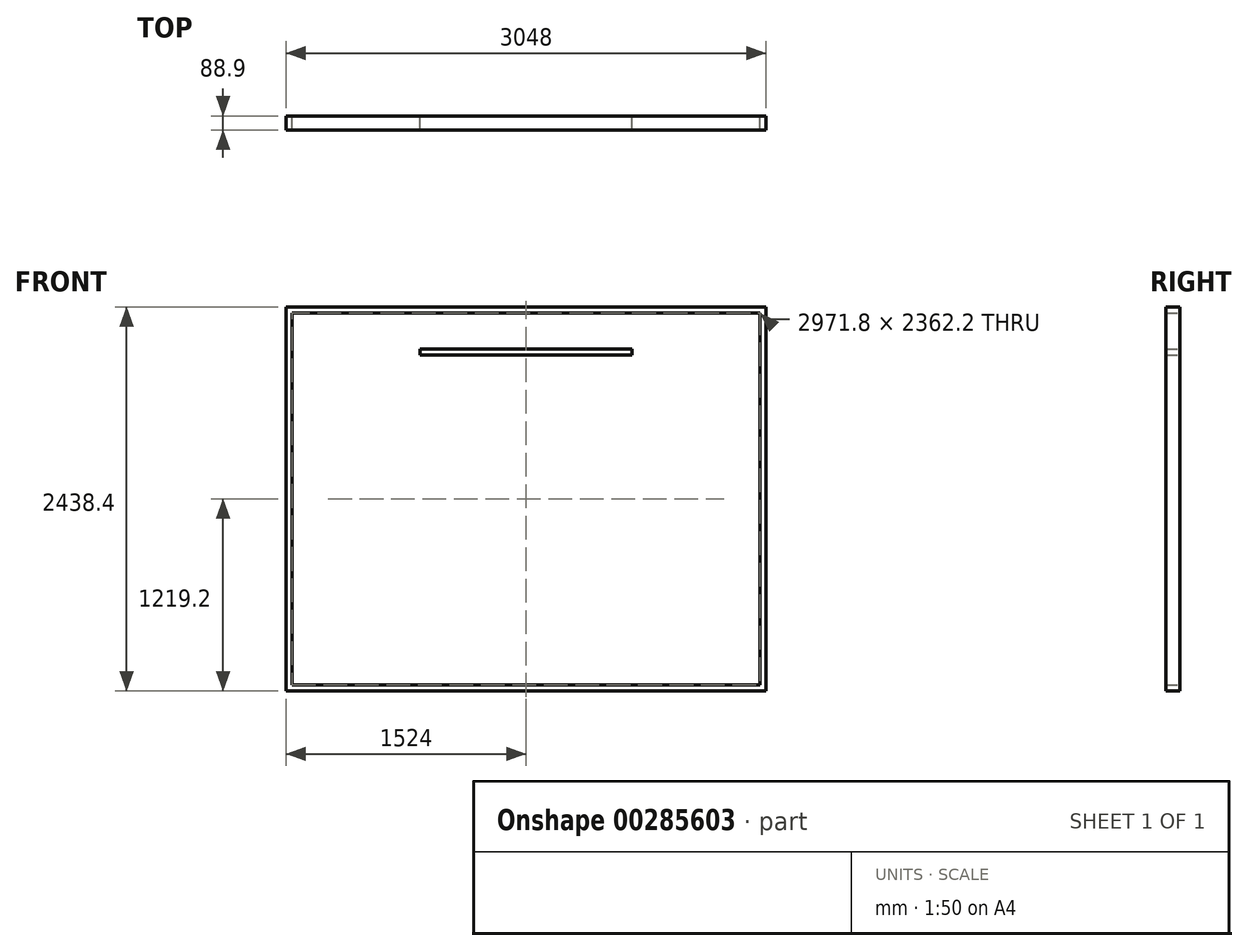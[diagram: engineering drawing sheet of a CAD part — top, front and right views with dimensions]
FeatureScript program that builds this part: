
annotation { "Feature Type Name" : "Feature", "Feature Type Description" : "" }
export const myFeature = defineFeature(function(context is Context, id is Id, definition is map)
    precondition{}
    {
        {
            var Q0;
            Q0=qCreatedBy(makeId("Front.planeOp"),FACE);
            var sketch = newSketch(context, id + "F0", { "sketchPlane" : qUnion([Q0])});
            skLineSegment(sketch, "E0.bottom", {"start": v(1485.9, -1219.2) * mm, "end": v(-1485.9, -1219.2) * mm});
            skLineSegment(sketch, "E0.left", {"start": v(1485.9, -1219.2) * mm, "end": v(1485.9, 1143) * mm});
            skLineSegment(sketch, "E0.right", {"start": v(-1485.9, -1219.2) * mm, "end": v(-1485.9, 1143) * mm});
            skPoint(sketch, "E0.middle", {"position": v(0, 0) * mm});
            skLineSegment(sketch, "E1.bottom", {"start": v(-1524, -1257.3) * mm, "end": v(1524, -1257.3) * mm});
            skLineSegment(sketch, "E1.left", {"start": v(-1524, -1257.3) * mm, "end": v(-1524, 1143) * mm});
            skLineSegment(sketch, "E1.right", {"start": v(1524, -1257.3) * mm, "end": v(1524, 1181.1) * mm});
            skLineSegment(sketch, "E2", {"start": v(1485.9, -1219.2) * mm, "end": v(1524, -1219.2) * mm});
            skLineSegment(sketch, "E3", {"start": v(-1485.9, -1219.2) * mm, "end": v(-1524, -1219.2) * mm});
            skLineSegment(sketch, "E4", {"start": v(-1524, -1219.2) * mm, "end": v(-1117.6, -1219.2) * mm});
            skLineSegment(sketch, "E5", {"start": v(-1117.6, -1219.2) * mm, "end": v(-711.2, -1219.2) * mm});
            skLineSegment(sketch, "E6", {"start": v(-711.2, -1219.2) * mm, "end": v(-304.8, -1219.2) * mm});
            skLineSegment(sketch, "E7", {"start": v(1524, -1219.2) * mm, "end": v(1117.6, -1219.2) * mm});
            skLineSegment(sketch, "E8", {"start": v(1117.6, -1219.2) * mm, "end": v(711.2, -1219.2) * mm});
            skLineSegment(sketch, "E9", {"start": v(711.2, -1219.2) * mm, "end": v(304.8, -1219.2) * mm});
            skLineSegment(sketch, "E10", {"start": v(304.8, -1219.2) * mm, "end": v(0, -1219.2) * mm});
            skLineSegment(sketch, "E11.bottom", {"start": v(-1117.6, -1219.2) * mm, "end": v(-1079.5, -1219.2) * mm});
            skLineSegment(sketch, "E11.left", {"start": v(-1117.6, -1219.2) * mm, "end": v(-1117.6, 1143) * mm});
            skLineSegment(sketch, "E11.right", {"start": v(-1079.5, -1219.2) * mm, "end": v(-1079.5, 1143) * mm});
            skLineSegment(sketch, "E12.bottom", {"start": v(-711.2, -1219.2) * mm, "end": v(-673.1, -1219.2) * mm});
            skLineSegment(sketch, "E12.left", {"start": v(-711.2, -1219.2) * mm, "end": v(-711.2, 1143) * mm});
            skLineSegment(sketch, "E13.bottom", {"start": v(1117.6, -1219.2) * mm, "end": v(1079.5, -1219.2) * mm});
            skLineSegment(sketch, "E13.left", {"start": v(1117.6, -1219.2) * mm, "end": v(1117.6, 1143) * mm});
            skLineSegment(sketch, "E13.right", {"start": v(1079.5, -1219.2) * mm, "end": v(1079.5, 1143) * mm});
            skLineSegment(sketch, "E14.bottom", {"start": v(711.2, -1219.2) * mm, "end": v(673.1, -1219.2) * mm});
            skLineSegment(sketch, "E14.left", {"start": v(711.2, -1219.2) * mm, "end": v(711.2, 1143) * mm});
            skLineSegment(sketch, "E15.top", {"start": v(673.1, -38.1) * mm, "end": v(-673.1, -38.1) * mm});
            skLineSegment(sketch, "E16.bottom", {"start": v(-673.1, -38.1) * mm, "end": v(673.1, -38.1) * mm});
            skLineSegment(sketch, "E16.top", {"start": v(-673.1, -76.2) * mm, "end": v(673.1, -76.2) * mm});
            skLineSegment(sketch, "E16.left", {"start": v(-673.1, -38.1) * mm, "end": v(-673.1, -76.2) * mm});
            skLineSegment(sketch, "E16.right", {"start": v(673.1, -38.1) * mm, "end": v(673.1, -76.2) * mm});
            skLineSegment(sketch, "E17.bottom", {"start": v(-304.8, -1219.2) * mm, "end": v(-266.7, -1219.2) * mm});
            skLineSegment(sketch, "E17.top", {"start": v(-304.8, -76.2) * mm, "end": v(-266.7, -76.2) * mm});
            skLineSegment(sketch, "E17.left", {"start": v(-304.8, -1219.2) * mm, "end": v(-304.8, -76.2) * mm});
            skLineSegment(sketch, "E17.right", {"start": v(-266.7, -1219.2) * mm, "end": v(-266.7, -76.2) * mm});
            skLineSegment(sketch, "E18.bottom", {"start": v(-266.7, -1219.2) * mm, "end": v(-228.6, -1219.2) * mm});
            skLineSegment(sketch, "E18.top", {"start": v(-266.7, -76.2) * mm, "end": v(-228.6, -76.2) * mm});
            skLineSegment(sketch, "E18.right", {"start": v(-228.6, -1219.2) * mm, "end": v(-228.6, -76.2) * mm});
            skLineSegment(sketch, "E19.bottom", {"start": v(304.8, -1219.2) * mm, "end": v(266.7, -1219.2) * mm});
            skLineSegment(sketch, "E19.top", {"start": v(304.8, -76.2) * mm, "end": v(266.7, -76.2) * mm});
            skLineSegment(sketch, "E19.left", {"start": v(304.8, -1219.2) * mm, "end": v(304.8, -76.2) * mm});
            skLineSegment(sketch, "E19.right", {"start": v(266.7, -1219.2) * mm, "end": v(266.7, -76.2) * mm});
            skLineSegment(sketch, "E20.bottom", {"start": v(266.7, -1219.2) * mm, "end": v(228.6, -1219.2) * mm});
            skLineSegment(sketch, "E20.top", {"start": v(266.7, -76.2) * mm, "end": v(228.6, -76.2) * mm});
            skLineSegment(sketch, "E20.right", {"start": v(228.6, -1219.2) * mm, "end": v(228.6, -76.2) * mm});
            skLineSegment(sketch, "E21", {"start": v(673.1, -1219.2) * mm, "end": v(673.1, 1143) * mm});
            skLineSegment(sketch, "E22", {"start": v(-673.1, 1143) * mm, "end": v(-673.1, -1219.2) * mm});
            skLineSegment(sketch, "E23.top", {"start": v(-673.1, 914.4) * mm, "end": v(673.1, 914.4) * mm});
            skLineSegment(sketch, "E23.left", {"start": v(-673.1, 1143) * mm, "end": v(-673.1, 914.4) * mm});
            skLineSegment(sketch, "E23.right", {"start": v(673.1, 1143) * mm, "end": v(673.1, 914.4) * mm});
            skLineSegment(sketch, "E24.top", {"start": v(-673.1, 876.3) * mm, "end": v(673.1, 876.3) * mm});
            skLineSegment(sketch, "E24.left", {"start": v(-673.1, 914.4) * mm, "end": v(-673.1, 876.3) * mm});
            skLineSegment(sketch, "E24.right", {"start": v(673.1, 914.4) * mm, "end": v(673.1, 876.3) * mm});
            skLineSegment(sketch, "E25.bottom", {"start": v(-673.1, -38.1) * mm, "end": v(-571.5, -38.1) * mm});
            skLineSegment(sketch, "E25.top", {"start": v(-673.1, 876.3) * mm, "end": v(-571.5, 876.3) * mm});
            skLineSegment(sketch, "E25.left", {"start": v(-673.1, -38.1) * mm, "end": v(-673.1, 876.3) * mm});
            skLineSegment(sketch, "E25.right", {"start": v(-571.5, -38.1) * mm, "end": v(-571.5, 876.3) * mm});
            skLineSegment(sketch, "E26.bottom", {"start": v(-571.5, -38.1) * mm, "end": v(-533.4, -38.1) * mm});
            skLineSegment(sketch, "E26.top", {"start": v(-571.5, 876.3) * mm, "end": v(-533.4, 876.3) * mm});
            skLineSegment(sketch, "E26.right", {"start": v(-533.4, -38.1) * mm, "end": v(-533.4, 876.3) * mm});
            skLineSegment(sketch, "E27.bottom", {"start": v(673.1, -38.1) * mm, "end": v(571.5, -38.1) * mm});
            skLineSegment(sketch, "E27.top", {"start": v(673.1, 876.3) * mm, "end": v(571.5, 876.3) * mm});
            skLineSegment(sketch, "E27.left", {"start": v(673.1, -38.1) * mm, "end": v(673.1, 876.3) * mm});
            skLineSegment(sketch, "E27.right", {"start": v(571.5, -38.1) * mm, "end": v(571.5, 876.3) * mm});
            skLineSegment(sketch, "E28.bottom", {"start": v(571.5, -38.1) * mm, "end": v(533.4, -38.1) * mm});
            skLineSegment(sketch, "E28.top", {"start": v(571.5, 876.3) * mm, "end": v(533.4, 876.3) * mm});
            skLineSegment(sketch, "E28.right", {"start": v(533.4, -38.1) * mm, "end": v(533.4, 876.3) * mm});
            skLineSegment(sketch, "E29.top", {"start": v(-1524, 1143) * mm, "end": v(1524, 1143) * mm});
            skLineSegment(sketch, "E29.left", {"start": v(-1524, 1181.1) * mm, "end": v(-1524, 1143) * mm});
            skLineSegment(sketch, "E29.right", {"start": v(1524, 1181.1) * mm, "end": v(1524, 1143) * mm});
            skLineSegment(sketch, "E30.top", {"start": v(-1524, 1181.1) * mm, "end": v(1524, 1181.1) * mm});
            skLineSegment(sketch, "E30.left", {"start": v(-1524, 1143) * mm, "end": v(-1524, 1181.1) * mm});
            skLineSegment(sketch, "E30.right", {"start": v(1524, 1143) * mm, "end": v(1524, 1181.1) * mm});
            skPoint(sketch, "E31.orphan", {"position": v(-1524, 1257.3) * mm});
            skPoint(sketch, "E32.orphan", {"position": v(-1485.9, 1219.2) * mm});
            skPoint(sketch, "E33.orphan", {"position": v(-673.1, 1219.2) * mm});
            skPoint(sketch, "E34.orphan", {"position": v(1524, 1219.2) * mm});
            skPoint(sketch, "E35.orphan", {"position": v(1524, 1257.3) * mm});
            skPoint(sketch, "E36.orphan", {"position": v(1485.9, 1219.2) * mm});
            skSolve(sketch);
        }
        {
            var Q0;
            {var subQ0=sQuery(id+"F0.wireOp",EDGE,"E0.right");Q0=makeQuery(id+"F0.imprint","IMPRINT",FACE,{"disambiguationData":[TD([[makeQuery(id+"F0.imprint","IMPRINT",EDGE,{"derivedFrom":subQ0}),1.0]])]});}
            var Q1;
            {var subQ1=sQuery(id+"F0.wireOp",EDGE,"E1.top");Q1=makeQuery(id+"F0.imprint","IMPRINT",FACE,{"disambiguationData":[TD([[makeQuery(id+"F0.imprint","IMPRINT",EDGE,{"derivedFrom":subQ1}),-1.0]])]});}
            var Q2;
            Q2=makeQuery(id+"F0.imprint","IMPRINT",FACE,{"disambiguationData":[TD([[makeQuery(id+"F0.imprint","IMPRINT",EDGE,{"derivedFrom":sQuery(id+"F0.wireOp",EDGE,"E11.bottom")}),1.0]])]});
            var Q3;
            {var subQ3=sQuery(id+"F0.wireOp",EDGE,"E12.bottom");Q3=makeQuery(id+"F0.imprint","IMPRINT",FACE,{"disambiguationData":[TD([[makeQuery(id+"F0.imprint","IMPRINT",EDGE,{"derivedFrom":subQ3}),1.0]])]});}
            var Q4;
            Q4=makeQuery(id+"F0.imprint","IMPRINT",FACE,{"disambiguationData":[TD([[makeQuery(id+"F0.imprint","IMPRINT",EDGE,{"derivedFrom":sQuery(id+"F0.wireOp",EDGE,"E23.top")}),-1.0]])]});
            var Q5;
            Q5=makeQuery(id+"F0.imprint","IMPRINT",FACE,{"disambiguationData":[TD([[makeQuery(id+"F0.imprint","IMPRINT",EDGE,{"derivedFrom":sQuery(id+"F0.wireOp",EDGE,"E26.bottom")}),1.0]])]});
            var Q6;
            Q6=makeQuery(id+"F0.imprint","IMPRINT",FACE,{"disambiguationData":[TD([[makeQuery(id+"F0.imprint","IMPRINT",EDGE,{"derivedFrom":sQuery(id+"F0.wireOp",EDGE,"E28.bottom")}),-1.0]])]});
            var Q7;
            {var subQ2=sQuery(id+"F0.wireOp",EDGE,"E14.bottom");Q7=makeQuery(id+"F0.imprint","IMPRINT",FACE,{"disambiguationData":[TD([[makeQuery(id+"F0.imprint","IMPRINT",EDGE,{"derivedFrom":subQ2}),-1.0]])]});}
            var Q8;
            Q8=makeQuery(id+"F0.imprint","IMPRINT",FACE,{"disambiguationData":[TD([[makeQuery(id+"F0.imprint","IMPRINT",EDGE,{"derivedFrom":sQuery(id+"F0.wireOp",EDGE,"E16.bottom")}),-1.0]])]});
            var Q9;
            Q9=makeQuery(id+"F0.imprint","IMPRINT",FACE,{"disambiguationData":[TD([[makeQuery(id+"F0.imprint","IMPRINT",EDGE,{"derivedFrom":sQuery(id+"F0.wireOp",EDGE,"E19.bottom")}),-1.0]])]});
            var Q10;
            Q10=makeQuery(id+"F0.imprint","IMPRINT",FACE,{"disambiguationData":[TD([[makeQuery(id+"F0.imprint","IMPRINT",EDGE,{"derivedFrom":sQuery(id+"F0.wireOp",EDGE,"E20.bottom")}),-1.0]])]});
            var Q11;
            Q11=makeQuery(id+"F0.imprint","IMPRINT",FACE,{"disambiguationData":[TD([[makeQuery(id+"F0.imprint","IMPRINT",EDGE,{"derivedFrom":sQuery(id+"F0.wireOp",EDGE,"E18.bottom")}),1.0]])]});
            var Q12;
            Q12=makeQuery(id+"F0.imprint","IMPRINT",FACE,{"disambiguationData":[TD([[makeQuery(id+"F0.imprint","IMPRINT",EDGE,{"derivedFrom":sQuery(id+"F0.wireOp",EDGE,"E17.bottom")}),1.0]])]});
            var Q13;
            Q13=makeQuery(id+"F0.imprint","IMPRINT",FACE,{"disambiguationData":[TD([[makeQuery(id+"F0.imprint","IMPRINT",EDGE,{"derivedFrom":sQuery(id+"F0.wireOp",EDGE,"E0.bottom")}),1.0]])]});
            var Q14;
            Q14=makeQuery(id+"F0.imprint","IMPRINT",FACE,{"disambiguationData":[TD([[makeQuery(id+"F0.imprint","IMPRINT",EDGE,{"derivedFrom":sQuery(id+"F0.wireOp",EDGE,"E13.bottom")}),-1.0]])]});
            var Q15;
            {var subQ0=sQuery(id+"F0.wireOp",EDGE,"E0.left");Q15=makeQuery(id+"F0.imprint","IMPRINT",FACE,{"disambiguationData":[TD([[makeQuery(id+"F0.imprint","IMPRINT",EDGE,{"derivedFrom":subQ0}),-1.0]])]});}
            var Q16;
            Q16=makeQuery(id+"F0.imprint","IMPRINT",FACE,{"disambiguationData":[TD([[makeQuery(id+"F0.imprint","IMPRINT",EDGE,{"derivedFrom":sQuery(id+"F0.wireOp",EDGE,"E30.top")}),-1.0]])]});
            extrude(context, id + "F1", {"entities" : qUnion([Q0, Q1, Q2, Q3, Q4, Q5, Q6, Q7, Q8, Q9, Q10, Q11, Q12, Q13, Q14, Q15, Q16]), "depth" : 88.9 * mm});
        }
    });
